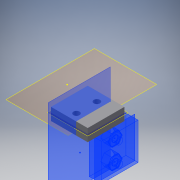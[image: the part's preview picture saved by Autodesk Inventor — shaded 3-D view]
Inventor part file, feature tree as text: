
AUTODESK INVENTOR PART (.ipt)
format: ipt  version: 2016 (Build 200138000, 138)  size: 146,432 bytes
history: native  units: mm
features: sketch x4, plane x2, extrude x2, projected_geometry x2, hole x1, reference x1
ambient origin geometry x8: Origin, YZ Plane, XZ Plane, XY Plane, X Axis, Y Axis, Z Axis, Center Point
bodies: Solid1 (feature_tree)
feature tree (12):
  plane  "Work Plane1"
  extrude  "Extrusion1"  Depth=18.0mm
  hole  "Hole1"  [1 undecoded]
  sketch  "Sketch3"  dims[d5=3.5mm d6=10.0mm]
  plane  "Work Plane2"
  sketch  "Sketch4"  dims[d7=3.0mm d8=6.0mm d9=4.0mm d10=2.0mm d11=90.0deg d12=8.0mm d13=20.594885mm d14=5.7mm d15=-3.5mm d16=4.0mm d17=0.0mm]
  extrude  "Extrusion2"  Depth=10.0mm
  sketch  "Sketch1"  dims[d0=9.0mm d1=18.0mm]
  reference  "Reference1"
  sketch  "Sketch2"  dims[d2=9.0mm d3=6.0mm d4=0.0mm]
  projected_geometry  "Projected Loop1"
  projected_geometry  "Projected Loop2"
note: 1 required parameter value undecoded (feature->parameter linkage not recoverable at this tier; creation-order binding heuristic only, values carry confidence <= 0.55)
